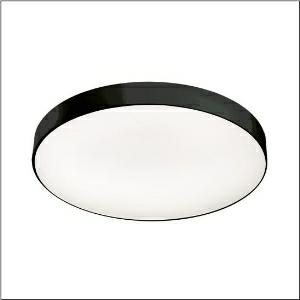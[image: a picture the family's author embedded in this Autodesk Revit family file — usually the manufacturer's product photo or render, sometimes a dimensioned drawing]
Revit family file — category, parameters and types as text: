
# Revit family: round_21_l_51mr38nd0321b
name_source: partatom
category: Lighting Fixtures
units: mm (PartAtom-declared; Revit-internal decimal feet)

## family parameters
Cut with Voids When Loaded = No
Host = Face
Light Source = No
Part Type = Normal
Room Calculation Point = No
Round Connector Dimension = Use Diameter
Shared = No

## types (1)
- Round 21 L (1 x LED, 11740 lm, 88.2 W, 3000K)
    Apparent Load = 88 VA
    CIE Flux Codes = 66 90 98 71 100
    Color Rendering = 80
    Color Temperature = 3000K
    Default Elevation = 1800 mm
    Description = Round 21 L, wall and ceiling luminaire, primary optical cover: micro prismatic cover, of PMMA, transparent, CAT 2 (L<= 3000cd/m²), light emission: direct/indirect distribution, primary light characteristic: symmetric, installation type: suspended mounting, surface-mounted, LED, rated luminous flux: 11.740lm, luminous efficacy: 133lm/W, light colour: 830, colour temperature: 3000K, control gear: DALI 2, with terminal, 5-pole, mains connection: 230V, AC, 50/60Hz, rated input power: 88.2W, housing, of aluminium, coated, black, diameter: 850mm, height: 62mm, protection rating (complete): IP40, insulation class (complete): insulation class I (protective earthing), certification: CE, impact resistance: IK04, permissible operating ambient temperature: -10..+35°C, packaging unit: 1 piece
    Height = 87 mm
    Lamp = 1 x LED
    Lamp Light Flux = 11740 lm
    Lamp Power = 88.2 W
    Lamp count = 1
    Length = 850 mm
    Luminous efficacy = 133 lm/W
    Manufacturer = Siteco
    ModVariant = No
    Model = 51MR38ND0321B
    Mounting Place = Ceiling
    Mounting Type = Surface mounted
    Number of Poles = 1
    OnlyDefault = Yes
    Power Factor = 1
    Product Name = Round 21 L
    Product group = wall and ceiling luminaire | ceiling mounted
    ProductGroupID = 304
    Protection Class = Protection class I
    Protection Degree = IP 40
    RLX_Detail_Level = 1
    RLX_Emergency_Light_Flux = 0 lm
    RLX_Emergency_Type = 0
    RLX_Emergency_Type_DB = No
    RlxData = <blob elided: 28725 chars, md5=34ef071f>
    Socket = socket
    Standby Power = 0 W
    System Light Flux = 11740 lm
    System Power = 88 W
    Type Comments = Product without accessories
    Type Image = l_1258326.jpg
    URL = http://relux.com
    VarID = ---
    Voltage = 0 V
    Weight = 0.00 kg
    Width = 0 mm  [stored 0 ft]

note: [stored X ft] marks values corroborated as IEEE doubles in the binary element streams (Revit-internal decimal feet)

## geometry (parser evidence)
native form markers: Blend x4, Sweep x14
no freeform markers — native parametric forms only
